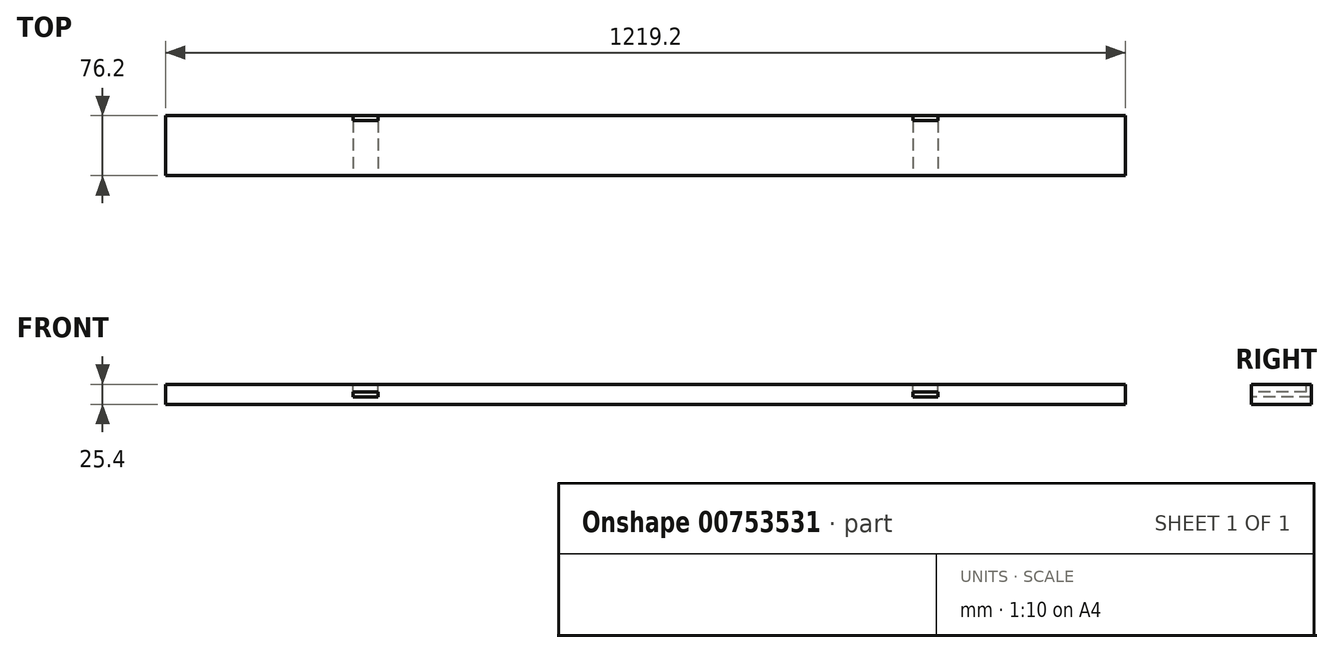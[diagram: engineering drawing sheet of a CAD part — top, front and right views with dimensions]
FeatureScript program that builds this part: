
annotation { "Feature Type Name" : "Feature", "Feature Type Description" : "" }
export const myFeature = defineFeature(function(context is Context, id is Id, definition is map)
    precondition{}
    {
        {
            var Q0;
            Q0=qCreatedBy(makeId("Top.planeOp"),FACE);
            var sketch = newSketch(context, id + "F0", { "sketchPlane" : qUnion([Q0])});
            skLineSegment(sketch, "E0.bottom", {"start": v(609.6, -38.1) * mm, "end": v(-609.6, -38.1) * mm});
            skLineSegment(sketch, "E0.top", {"start": v(609.6, 38.1) * mm, "end": v(-609.6, 38.1) * mm});
            skLineSegment(sketch, "E0.left", {"start": v(609.6, -38.1) * mm, "end": v(609.6, 38.1) * mm});
            skLineSegment(sketch, "E0.right", {"start": v(-609.6, -38.1) * mm, "end": v(-609.6, 38.1) * mm});
            skPoint(sketch, "E0.middle", {"position": v(0, 0) * mm});
            skSolve(sketch);
        }
        {
            var Q0;
            Q0=makeQuery(id+"F0.imprint","IMPRINT",FACE,{"disambiguationData":[TD([[makeQuery(id+"F0.imprint","IMPRINT",EDGE,{"derivedFrom":sQuery(id+"F0.wireOp",EDGE,"E0.bottom")}),-1.0]])]});
            extrude(context, id + "F1", {"entities" : qUnion([Q0]), "endBound" : BoundingType.SYMMETRIC, "depth" : 25.4 * mm, "offsetDistance" : 25.4 * mm});
        }
        {
            var Q0;
            Q0=makeQuery(id+"F1.opExtrude","SWEPT_FACE",FACE,{"disambiguationData":[OSD([sQuery(id+"F0.wireOp",EDGE,"E0.bottom")])]});
            var sketch = newSketch(context, id + "F2", { "sketchPlane" : qUnion([Q0])});
            skLineSegment(sketch, "E1.bottom", {"start": v(-339.73, 3.17) * mm, "end": v(-371.48, 3.17) * mm});
            skLineSegment(sketch, "E1.top", {"start": v(-339.73, -3.18) * mm, "end": v(-371.48, -3.18) * mm});
            skLineSegment(sketch, "E1.left", {"start": v(-339.73, 3.17) * mm, "end": v(-339.73, -3.18) * mm});
            skLineSegment(sketch, "E1.right", {"start": v(-371.48, 3.17) * mm, "end": v(-371.48, -3.18) * mm});
            skPoint(sketch, "E1.middle", {"position": v(-355.6, 0) * mm});
            skLineSegment(sketch, "E2.MirrorCS", {"start": v(339.73, 3.17) * mm, "end": v(371.48, 3.17) * mm});
            skLineSegment(sketch, "E3.MirrorCS", {"start": v(371.48, 3.17) * mm, "end": v(371.48, -3.18) * mm});
            skLineSegment(sketch, "E4.MirrorCS", {"start": v(339.73, -3.18) * mm, "end": v(371.48, -3.18) * mm});
            skLineSegment(sketch, "E5.MirrorCS", {"start": v(339.73, 3.17) * mm, "end": v(339.73, -3.18) * mm});
            skSolve(sketch);
        }
        {
            var Q0;
            Q0=makeQuery(id+"F2.imprint","IMPRINT",FACE,{"disambiguationData":[TD([[makeQuery(id+"F2.imprint","IMPRINT",EDGE,{"derivedFrom":sQuery(id+"F2.wireOp",EDGE,"E1.bottom")}),1.0]])]});
            extrude(context, id + "F3", {"entities" : qUnion([Q0]), "operationType" : NewBodyOperationType.REMOVE, "endBound" : BoundingType.UP_TO_NEXT, "oppositeDirection" : true, "depth" : 25.4 * mm, "offsetDistance" : 25.4 * mm});
        }
        {
            var Q0;
            Q0=makeQuery(id+"F2.imprint","IMPRINT",FACE,{"disambiguationData":[TD([[makeQuery(id+"F2.imprint","IMPRINT",EDGE,{"derivedFrom":sQuery(id+"F2.wireOp",EDGE,"E2.MirrorCS")}),-1.0]])]});
            extrude(context, id + "F4", {"entities" : qUnion([Q0]), "operationType" : NewBodyOperationType.REMOVE, "endBound" : BoundingType.UP_TO_NEXT, "oppositeDirection" : true, "depth" : 25.4 * mm, "offsetDistance" : 25.4 * mm});
        }
        {
            var Q0;
            Q0=makeQuery(id+"F1.opExtrude","CAP_FACE",FACE,{"disambiguationData":[OSD([sQuery(id+"F0.wireOp",EDGE,"E0.bottom"),sQuery(id+"F0.wireOp",EDGE,"E0.top"),sQuery(id+"F0.wireOp",EDGE,"E0.left"),sQuery(id+"F0.wireOp",EDGE,"E0.right")])],"isStart":false});
            var sketch = newSketch(context, id + "F5", { "sketchPlane" : qUnion([Q0])});
            skLineSegment(sketch, "E6.bottom", {"start": v(-371.48, 38.1) * mm, "end": v(-339.73, 38.1) * mm});
            skLineSegment(sketch, "E6.top", {"start": v(-371.48, 31.75) * mm, "end": v(-339.73, 31.75) * mm});
            skLineSegment(sketch, "E6.left", {"start": v(-371.48, 38.1) * mm, "end": v(-371.48, 31.75) * mm});
            skLineSegment(sketch, "E6.right", {"start": v(-339.73, 38.1) * mm, "end": v(-339.73, 31.75) * mm});
            skLineSegment(sketch, "E7.MirrorCS", {"start": v(339.73, 38.1) * mm, "end": v(339.73, 31.75) * mm});
            skLineSegment(sketch, "E8.MirrorCS", {"start": v(371.48, 38.1) * mm, "end": v(339.73, 38.1) * mm});
            skLineSegment(sketch, "E9.MirrorCS", {"start": v(371.48, 38.1) * mm, "end": v(371.48, 31.75) * mm});
            skLineSegment(sketch, "E10.MirrorCS", {"start": v(371.48, 31.75) * mm, "end": v(339.73, 31.75) * mm});
            skSolve(sketch);
        }
        {
            var Q0;
            Q0=makeQuery(id+"F5.imprint","IMPRINT",FACE,{"disambiguationData":[TD([[makeQuery(id+"F5.imprint","IMPRINT",EDGE,{"derivedFrom":sQuery(id+"F5.wireOp",EDGE,"E6.bottom")}),1.0]])]});
            extrude(context, id + "F6", {"entities" : qUnion([Q0]), "operationType" : NewBodyOperationType.REMOVE, "endBound" : BoundingType.UP_TO_NEXT, "oppositeDirection" : true, "depth" : 25.4 * mm, "offsetDistance" : 25.4 * mm});
        }
        {
            var Q0;
            Q0=makeQuery(id+"F5.imprint","IMPRINT",FACE,{"disambiguationData":[TD([[makeQuery(id+"F5.imprint","IMPRINT",EDGE,{"derivedFrom":sQuery(id+"F5.wireOp",EDGE,"E7.MirrorCS")}),1.0]])]});
            extrude(context, id + "F7", {"entities" : qUnion([Q0]), "operationType" : NewBodyOperationType.REMOVE, "endBound" : BoundingType.UP_TO_NEXT, "oppositeDirection" : true, "depth" : 25.4 * mm, "offsetDistance" : 25.4 * mm});
        }
    });
